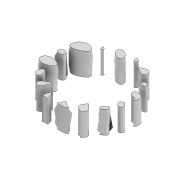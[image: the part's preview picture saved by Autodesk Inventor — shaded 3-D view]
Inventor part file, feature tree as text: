
AUTODESK INVENTOR PART (.ipt)
format: ipt  version: 2021 (Build 250183000, 183)  size: 242,688 bytes
history: native  units: in
note: dims shown in document units (in); Inventor stores cm internally (conversion verified against a paired STEP export)
features: extrude x1, mirror x1, sketch x1
ambient origin geometry x8: Origin, YZ Plane, XZ Plane, XY Plane, X Axis, Y Axis, Z Axis, Center Point
bodies: Body1 (feature_tree)
feature tree (3):
  extrude  "Extrusion2"  Depth=6.2992in TaperAngle=360.0deg
  mirror  "Mirror1"
  sketch  "Sketch1"  dims[d1=0.0773in d2=6.2992in d4=360.0deg d8=118.1102in d9=0.0in]
